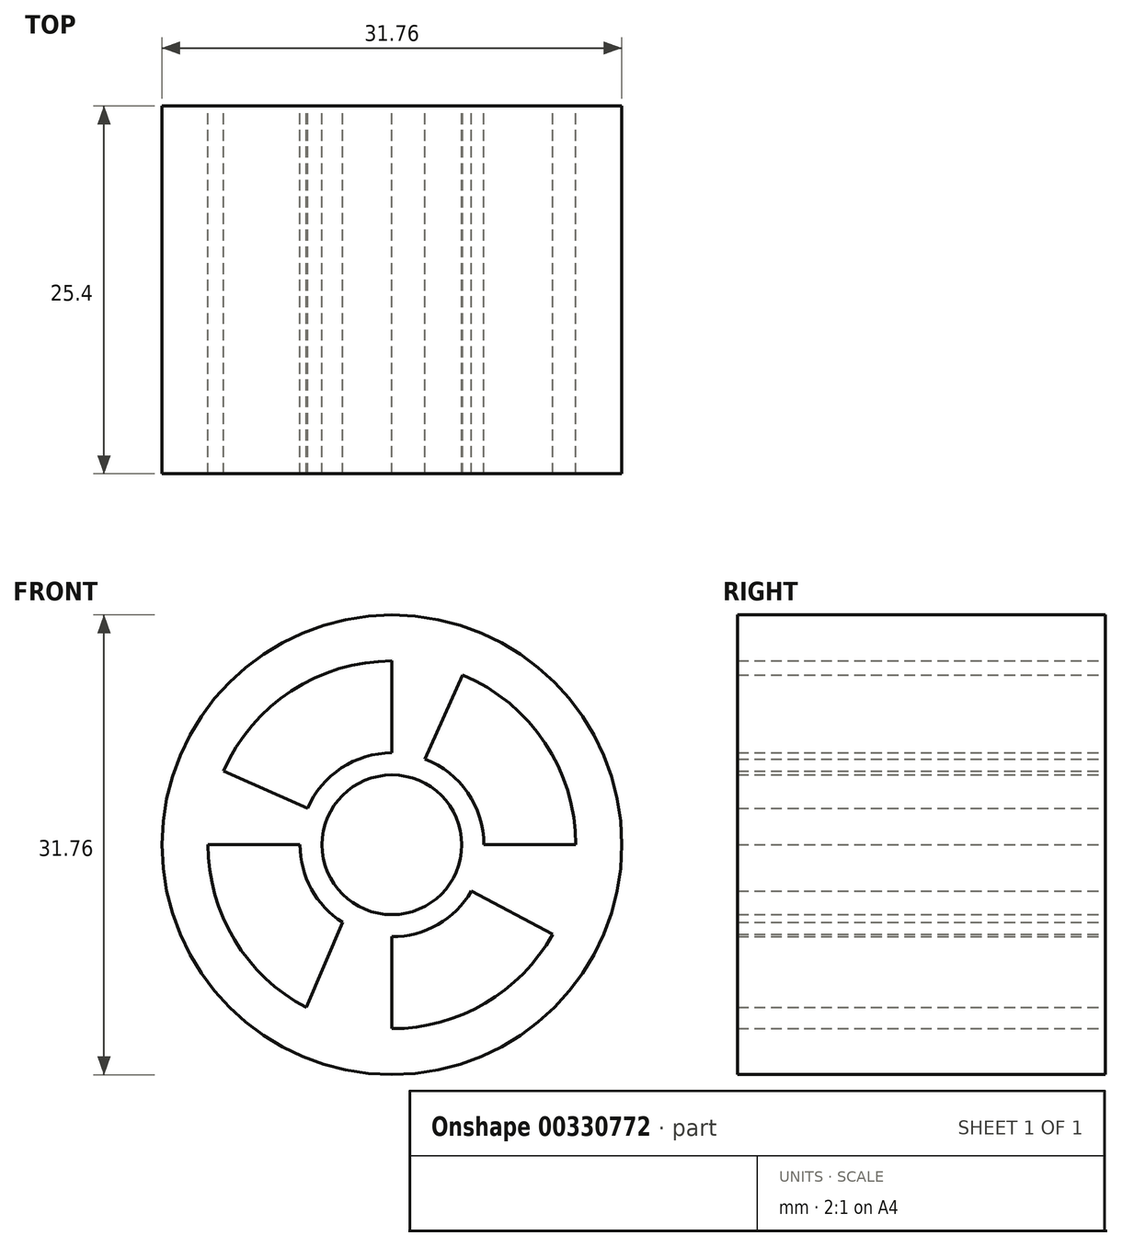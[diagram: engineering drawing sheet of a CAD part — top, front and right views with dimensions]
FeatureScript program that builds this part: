
annotation { "Feature Type Name" : "Feature", "Feature Type Description" : "" }
export const myFeature = defineFeature(function(context is Context, id is Id, definition is map)
    precondition{}
    {
        {
            var Q0;
            Q0=qCreatedBy(makeId("Front.planeOp"),FACE);
            var sketch = newSketch(context, id + "F0", { "sketchPlane" : qUnion([Q0])});
            skCircle(sketch, "E0", {"center": v(0, 0) * mm, "radius": 12.7 * mm});
            skCircle(sketch, "E1", {"center": v(0, 0) * mm, "radius": 6.35 * mm});
            skLineSegment(sketch, "E2", {"start": v(0, 6.35) * mm, "end": v(0, 12.7) * mm});
            skLineSegment(sketch, "E3", {"start": v(2.28, 5.93) * mm, "end": v(4.9, 11.72) * mm});
            skLineSegment(sketch, "E4", {"start": v(6.35, 0) * mm, "end": v(12.7, 0) * mm});
            skLineSegment(sketch, "E5", {"start": v(5.48, -3.2) * mm, "end": v(11.1, -6.19) * mm});
            skLineSegment(sketch, "E6", {"start": v(0, -6.35) * mm, "end": v(0, -12.7) * mm});
            skLineSegment(sketch, "E7", {"start": v(-3.42, -5.35) * mm, "end": v(-5.91, -11.24) * mm});
            skLineSegment(sketch, "E8", {"start": v(-6.35, 0) * mm, "end": v(-12.7, 0) * mm});
            skLineSegment(sketch, "E9", {"start": v(-5.83, 2.5) * mm, "end": v(-11.63, 5.1) * mm});
            skCircle(sketch, "E10", {"center": v(0, 0) * mm, "radius": 15.88 * mm});
            skCircle(sketch, "E11", {"center": v(0, 0) * mm, "radius": 4.83 * mm});
            skSolve(sketch);
        }
        {
            var Q0;
            Q0 = qSketchRegion(id + "F0", true);
            var Q1;
            {var subQ0=sQuery(id+"F0.wireOp",EDGE,"E2");Q1=makeQuery(id+"F0.imprint","IMPRINT",FACE,{"disambiguationData":[TD([[makeQuery(id+"F0.imprint","IMPRINT",EDGE,{"derivedFrom":subQ0}),-1.0]])]});}
            var Q2;
            {var subQ0=sQuery(id+"F0.wireOp",EDGE,"E8");Q2=makeQuery(id+"F0.imprint","IMPRINT",FACE,{"disambiguationData":[TD([[makeQuery(id+"F0.imprint","IMPRINT",EDGE,{"derivedFrom":subQ0}),-1.0]])]});}
            var Q3;
            {var subQ0=sQuery(id+"F0.wireOp",EDGE,"E6");Q3=makeQuery(id+"F0.imprint","IMPRINT",FACE,{"disambiguationData":[TD([[makeQuery(id+"F0.imprint","IMPRINT",EDGE,{"derivedFrom":subQ0}),-1.0]])]});}
            var Q4;
            {var subQ0=sQuery(id+"F0.wireOp",EDGE,"E4");Q4=makeQuery(id+"F0.imprint","IMPRINT",FACE,{"disambiguationData":[TD([[makeQuery(id+"F0.imprint","IMPRINT",EDGE,{"derivedFrom":subQ0}),-1.0]])]});}
            var Q5;
            Q5=makeQuery(id+"F0.imprint","IMPRINT",FACE,{"disambiguationData":[TD([[makeQuery(id+"F0.imprint","IMPRINT",EDGE,{"derivedFrom":sQuery(id+"F0.wireOp",EDGE,"E11")}),-1.0]])]});
            extrude(context, id + "F1", {"entities" : qUnion([Q0, Q1, Q2, Q3, Q4, Q5]), "depth" : 25.4 * mm});
        }
    });
